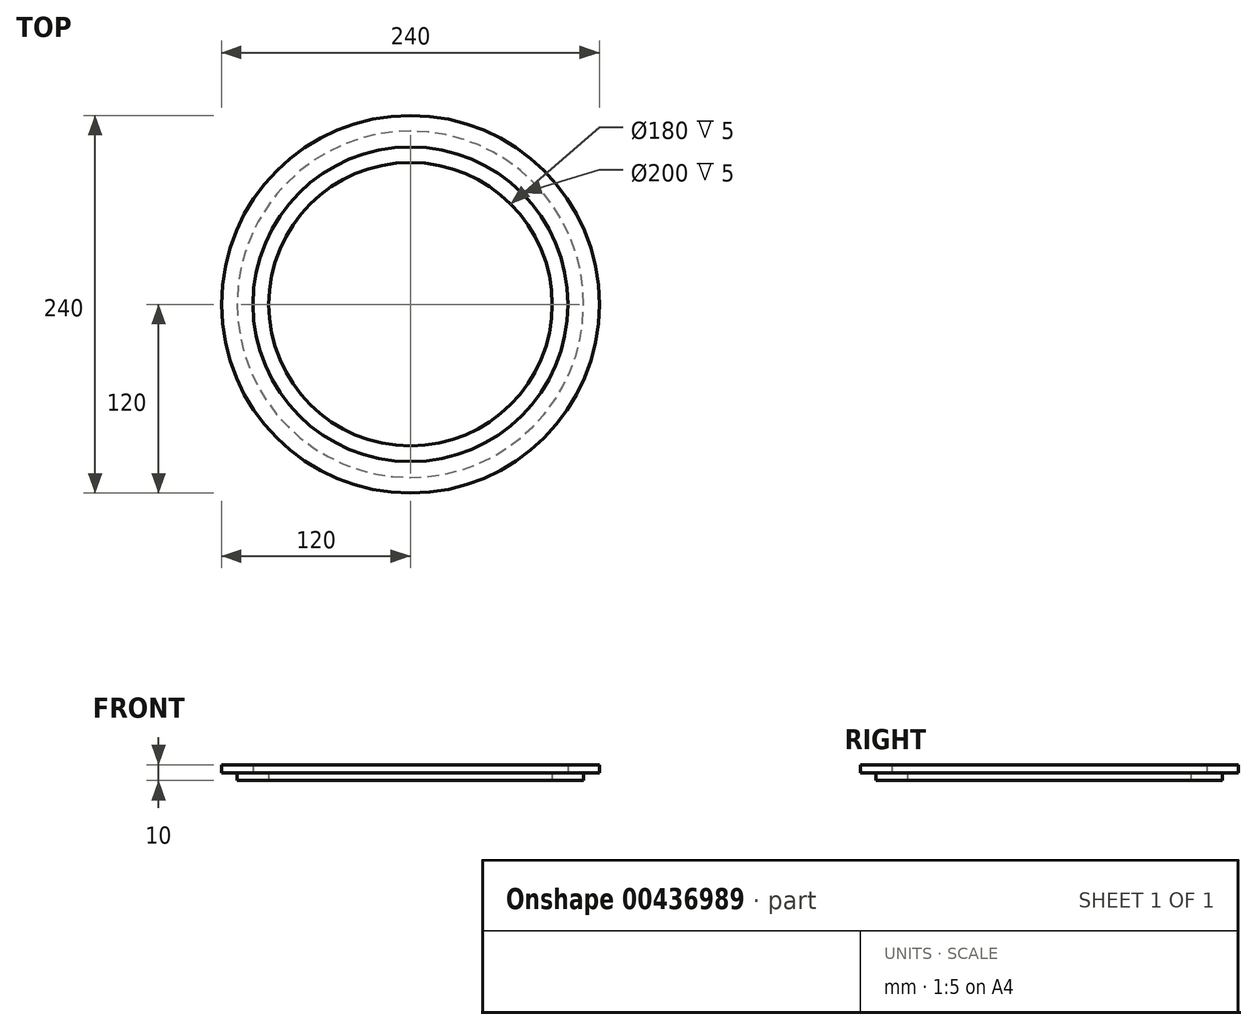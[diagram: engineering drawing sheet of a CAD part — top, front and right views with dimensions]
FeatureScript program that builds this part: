
annotation { "Feature Type Name" : "Feature", "Feature Type Description" : "" }
export const myFeature = defineFeature(function(context is Context, id is Id, definition is map)
    precondition{}
    {
        {
            var Q0;
            Q0=qCreatedBy(makeId("Front.planeOp"),FACE);
            var sketch = newSketch(context, id + "F0", { "sketchPlane" : qUnion([Q0])});
            skLineSegment(sketch, "E0", {"start": v(90, 0) * mm, "end": v(110, 0) * mm});
            skLineSegment(sketch, "E1", {"start": v(110, 0) * mm, "end": v(110, 5) * mm});
            skLineSegment(sketch, "E2", {"start": v(110, 5) * mm, "end": v(120, 5) * mm});
            skLineSegment(sketch, "E3", {"start": v(120, 5) * mm, "end": v(120, 10) * mm});
            skLineSegment(sketch, "E4", {"start": v(120, 10) * mm, "end": v(100, 10) * mm});
            skLineSegment(sketch, "E5", {"start": v(100, 10) * mm, "end": v(100, 5) * mm});
            skLineSegment(sketch, "E6", {"start": v(100, 5) * mm, "end": v(90, 5) * mm});
            skLineSegment(sketch, "E7", {"start": v(90, 5) * mm, "end": v(90, 0) * mm});
            skLineSegment(sketch, "E8", {"start": v(0, 0) * mm, "end": v(0, 62.26) * mm, "construction": true});
            skSolve(sketch);
        }
        {
            var Q0;
            Q0=makeQuery(id+"F0.imprint","IMPRINT",FACE,{"disambiguationData":[TD([[makeQuery(id+"F0.imprint","IMPRINT",EDGE,{"derivedFrom":sQuery(id+"F0.wireOp",EDGE,"E0")}),1.0]])]});
            var Q1;
            Q1=sQuery(id+"F0.wireOp",EDGE,"E8");
            revolve(context, id + "F1", {"entities" : qUnion([Q0]), "axis" : qUnion([Q1]), "revolveType" : RevolveType.FULL});
        }
    });
